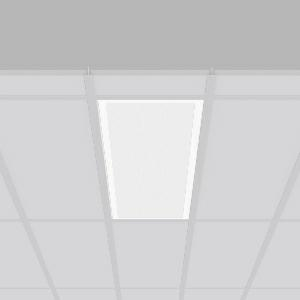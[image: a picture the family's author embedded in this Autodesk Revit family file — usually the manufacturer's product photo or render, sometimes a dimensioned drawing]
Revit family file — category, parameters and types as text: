
# Revit family: sidelite_eco_672374_002_1_04_1de9
name_source: partatom
category: Lighting Fixtures
units: mm (PartAtom-declared; Revit-internal decimal feet)

## family parameters
Cut with Voids When Loaded = No
Host = Face
Light Source = No
Part Type = Normal
Room Calculation Point = No
Round Connector Dimension = Use Diameter
Shared = No

## types (1)
- SIDELITE ECO (1 x LED Modul 840, 3500 lm, 4000)
    Apparent Load = 29 VA
    CIE Flux Codes = 59 87 97 100 100
    Color Rendering = 80
    Color Temperature = 4000
    Default Elevation = 1800 mm
    Description = Series: SIDELITE ECO
Highly economical recessed luminaire with progressive LED technology. For escape route illumination. Frame made of aluminium, powder-coated. Diffuser plastic microprismatic. Lightguide and diffuser made of non-yellowing plastic (PMMA). Lateral light emission (RZB SIDELITE technology) for homogeneous light distribution. External driver. Self-contained system with automatic self-test and feedback to the RZB monitoring system MULTIDIGIT. External driver with simple plug-in locking system. Extended connection cable (1.90 m). 
Colour: white
Length: 1245 mm
Width: 308 mm
Cut-out length: 1220 mm
Cut-out width: 285 mm
Recess height: 160 mm
Luminaire: recess height: 40 mm
Weight: 4.7 kg
Operating mode: maintained power mode
Duration time: 3 h
Lamp: LED
Socket: without socket
Colour temperature: 4000K
Colour rendering index (CRI): 80
System power: 29 W
Rated luminous flux: 3500 lm
Luminous flux, emergency: 510 lm
System power, emergency: -
Control gear: Regulated power supply
Protection class: I
Type of protection: IP 20
    Height = 0 mm  [stored 0 ft]
    Lamp = 1 x LED Modul 840
    Lamp Light Flux = 3500 lm
    Lamp count = 1
    Length = 1245 mm
    Lifetime = 50000 h
    Luminous efficacy = 121 lm/W
    Manufacturer = RZB
    ModVariant = No
    Model = 672374.002.1.04
    Mounting Place = Ceiling
    Mounting Type = Recessed
    Number of Poles = 1
    OnlyDefault = Yes
    Power Factor = 1
    Product Name = SIDELITE ECO
    Product group = Recessed modular luminaires
    ProductGroupID = 406
    Protection Class = Protection class I
    Protection Degree = IP 20
    RLX_Detail_Level = 1
    RLX_Emergency_Light_Flux = 510 lm
    RLX_Emergency_Type = 3
    RLX_Emergency_Type_DB = Yes
    RlxData = <blob elided: 34209 chars, md5=4e2d458a>
    Socket = socket
    Standby Power = 0 W
    System Light Flux = 3500 lm
    System Power = 29 W
    Type Comments = Product without accessories
    Type Image = 312368.002.jpg
    URL = http://relux.com
    VarID = ---
    Voltage = 230 V
    Voltage Range = 220-240 V
    Weight = 0.00 kg
    Width = 308 mm

note: [stored X ft] marks values corroborated as IEEE doubles in the binary element streams (Revit-internal decimal feet)

## geometry (parser evidence)
native form markers: Blend x4, Sweep x9
no freeform markers — native parametric forms only
